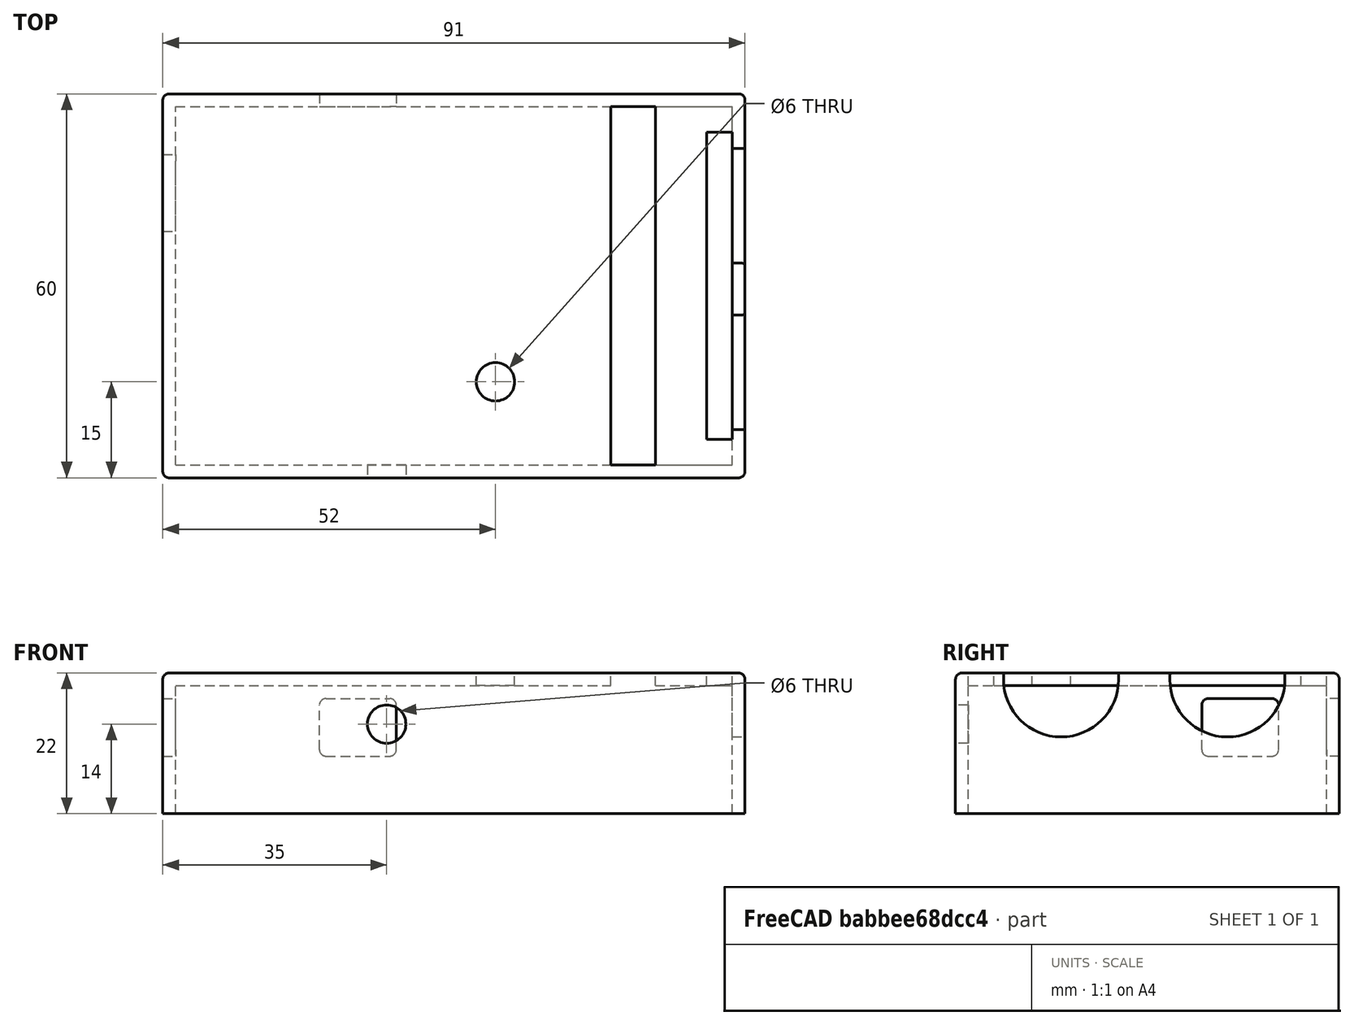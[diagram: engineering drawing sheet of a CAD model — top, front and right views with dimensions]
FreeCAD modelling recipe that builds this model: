
FCSTD DOCUMENT  (FreeCAD 0.15R4671 (Git))
Label: Galleta
License: All rights reserved
LicenseURL: http://en.wikipedia.org/wiki/All_rights_reserved
objects: Part::Fillet×7, Part::Box×6, Part::Cylinder×4, Part::Cut×2, Part::MultiFuse×1
note: 20 computed .brp shape members not serialized (recipe doc carries the construction recipe); baked Part::Feature solids carry a one-line shape summary decoded from their .brp

FEATURE [Part::Box] Box  label="Exterior"
  Height = 22
  Length = 91
  Width = 60
FEATURE [Part::Box] Box001  label="Interior"
  Height = 20
  Length = 87
  Placement = pos=(2,2,0) rot=(0,0,1;0rad)
  Width = 56
FEATURE [Part::Cut] Cut
  Base = -> Box
  Tool = -> Box001
FEATURE [Part::Fillet] Fillet
  Base = -> Cut
  Edges = 1 edges r=1: [Edge1]
FEATURE [Part::Fillet] Fillet001
  Base = -> Fillet
  Edges = 1 edges r=1: [Edge3]
FEATURE [Part::Fillet] Fillet002
  Base = -> Fillet001
  Edges = 1 edges r=1: [Edge22]
FEATURE [Part::Fillet] Fillet003
  Base = -> Fillet002
  Edges = 1 edges r=1: [Edge15]
FEATURE [Part::Fillet] Fillet004  label="BareTop"
  Base = -> Fillet003
  Edges = 1 edges r=1: [Edge5]
FEATURE [Part::Box] Box002  label="Cubo"
  Height = 2
  Length = 7
  Placement = pos=(70,2,20) rot=(0,0,1;0rad)
  Width = 56
FEATURE [Part::Cylinder] Cylinder  label="Cilindro"
  Angle = 360
  Height = 2
  Placement = pos=(35,2,14) rot=(1,0,0;1.5708rad)
  Radius = 3
FEATURE [Part::Cylinder] Cylinder001  label="Cilindro001"
  Angle = 360
  Height = 2
  Placement = pos=(52,15,20) rot=(0,0,1;0rad)
  Radius = 3
FEATURE [Part::Cylinder] Cylinder002  label="Cilindro002"
  Angle = 360
  Height = 2
  Placement = pos=(89,16.5,21) rot=(0,1,0;1.5708rad)
  Radius = 9
FEATURE [Part::Cylinder] Cylinder003  label="Cilindro003"
  Angle = 360
  Height = 2
  Placement = pos=(89,42.5,21) rot=(0,1,0;1.5708rad)
  Radius = 9
FEATURE [Part::Box] Box003  label="Cubo001"
  Height = 2
  Length = 4
  Placement = pos=(85,6,20) rot=(0,0,1;0rad)
  Width = 48
FEATURE [Part::Box] Box004  label="Cubo002"
  Height = 9
  Length = 2
  Placement = pos=(0,38.5,9) rot=(0,0,1;0rad)
  Width = 12
FEATURE [Part::MultiFuse] Fusion
  Shapes = -> [Cylinder001,Cylinder,Cylinder002,Cylinder003,Box003,Box002]
FEATURE [Part::Cut] Cut001
  Base = -> Fillet004
  Tool = -> Fusion
FEATURE [Part::Fillet] Fillet005
  Base = -> Box004
  Edges = 4 edges r=1: [Edge9,Edge10,Edge11,Edge12]
FEATURE [Part::Box] Box005  label="Cubo003"
  Height = 9
  Length = 2
  Placement = pos=(0,38.5,9) rot=(0,0,1;0rad)
  Width = 12
FEATURE [Part::Fillet] Fillet006
  Base = -> Box005
  Edges = 4 edges r=1: [Edge9,Edge10,Edge11,Edge12]
  Placement = pos=(-14,60,0) rot=(0,0,-1;1.5708rad)
